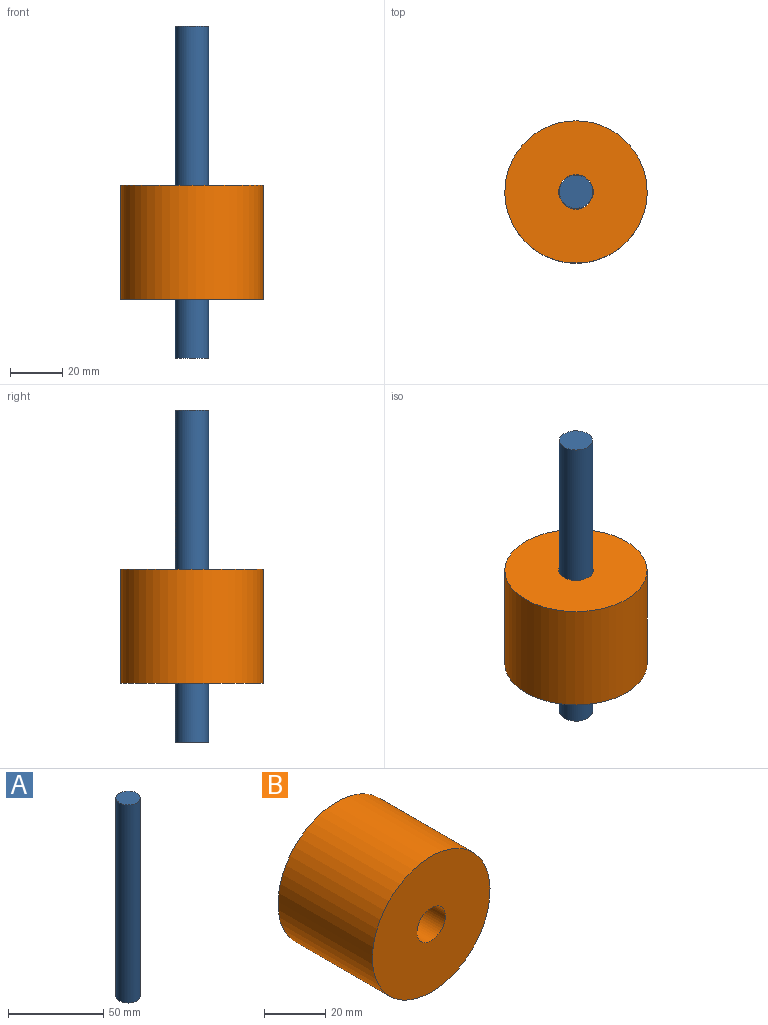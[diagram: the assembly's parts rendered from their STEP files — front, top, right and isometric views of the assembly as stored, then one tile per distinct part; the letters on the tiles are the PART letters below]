
ASSEMBLY  parts=2 mates=1
PART A: 3 faces, bbox 12.7x12.7x127 mm
  f0: cylinder r=6.35mm len=127mm, axis (0,0,1), area 5067.1mm2, adj f1,f2
  f1: plane 12.7x12.7mm, normal (0,0,-1), area 126.7mm2, adj f0
  f2: plane 12.7x12.7mm, normal (0,0,1), area 126.7mm2, adj f0
PART B: 4 faces, bbox 54.4x43.7x54.4 mm
  f0: cylinder r=27.22mm len=54.43mm, axis (0,1,0), area 7470.9mm2, adj f1,f2
  f1: plane 54.43x54.43mm, normal (0,-1,0), area 2190.1mm2, adj f0,f3
  f2: plane 54.43x54.43mm, normal (0,1,0), area 2190.1mm2, adj f0,f3
  f3: cylinder r=6.6mm len=43.69mm, axis (0,-1,0), area 1812.4mm2, adj f1,f2
PLACE A t=(90.58,10.91,102.63)mm fixed
PLACE B rot(axis=(1,0,0),90deg) t=(103.44,31.54,41.7)mm
MATE slider B.f0 <-> A.f0  axis (0,0,1) through (90.58,10.91,41.7)mm
